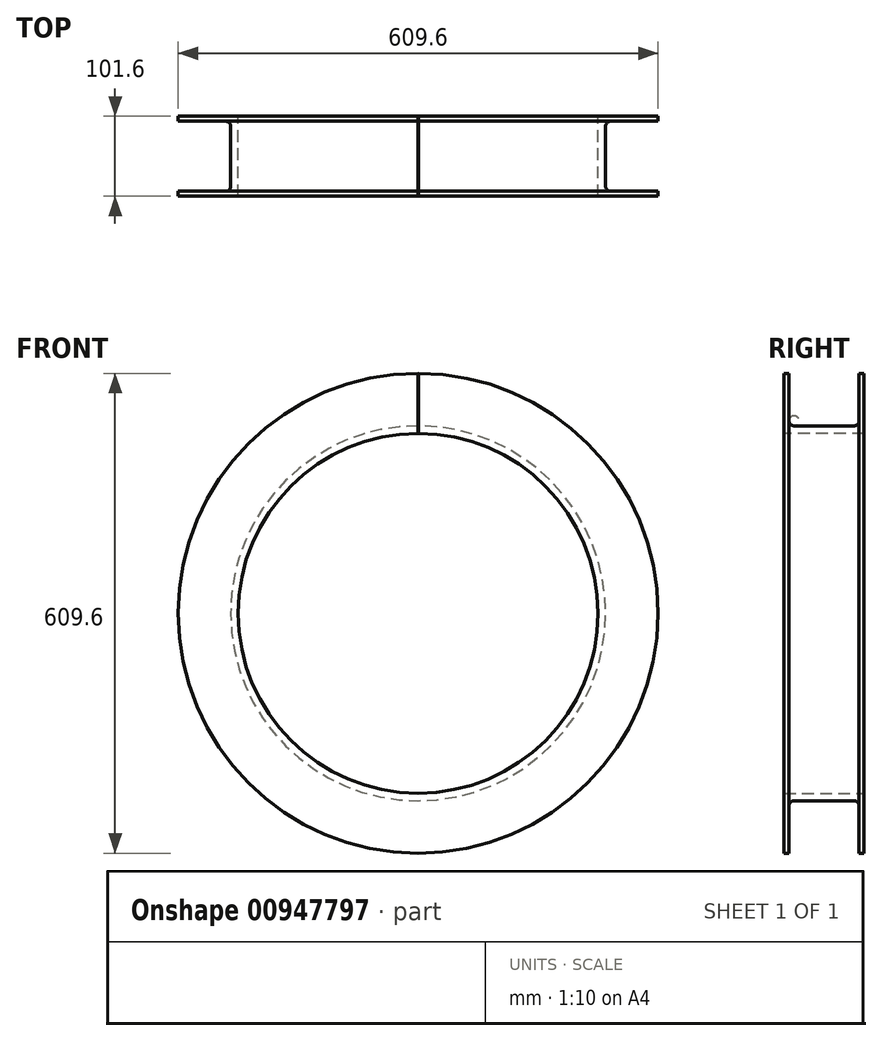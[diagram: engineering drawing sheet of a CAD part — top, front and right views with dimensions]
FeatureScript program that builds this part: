
annotation { "Feature Type Name" : "Feature", "Feature Type Description" : "" }
export const myFeature = defineFeature(function(context is Context, id is Id, definition is map)
    precondition{}
    {
        {
            var Q0;
            Q0=qCreatedBy(makeId("Right.planeOp"),FACE);
            var sketch = newSketch(context, id + "F0", { "sketchPlane" : qUnion([Q0])});
            skLineSegment(sketch, "E0", {"start": v(-118.17, 304.8) * mm, "end": v(123.28, 304.8) * mm, "construction": true});
            skLineSegment(sketch, "E1", {"start": v(0, 0) * mm, "end": v(0, 304.8) * mm, "construction": true});
            skLineSegment(sketch, "E2", {"start": v(0, 0) * mm, "end": v(-432.22, 0) * mm, "construction": true});
            skLineSegment(sketch, "E3.bottom", {"start": v(50.8, 228.6) * mm, "end": v(-50.8, 228.6) * mm});
            skLineSegment(sketch, "E3.left", {"start": v(50.8, 228.6) * mm, "end": v(50.8, 304.8) * mm});
            skLineSegment(sketch, "E3.right", {"start": v(-50.8, 228.6) * mm, "end": v(-50.8, 304.8) * mm});
            skPoint(sketch, "E3.middle", {"position": v(0, 304.8) * mm});
            skPoint(sketch, "E3.top.end.orphan", {"position": v(-50.8, 381) * mm});
            skPoint(sketch, "E4.orphan", {"position": v(50.8, 381) * mm});
            skLineSegment(sketch, "E5", {"start": v(44.45, 304.8) * mm, "end": v(44.45, 244.48) * mm});
            skLineSegment(sketch, "E6", {"start": v(38.1, 238.13) * mm, "end": v(-38.1, 238.13) * mm});
            skLineSegment(sketch, "E7", {"start": v(-44.45, 244.48) * mm, "end": v(-44.45, 304.8) * mm});
            skPoint(sketch, "E8.visualSharp", {"position": v(-44.45, 238.13) * mm});
            skArc(sketch, "E8.filletArc", {"start": v(-44.45, 244.48) * mm, "mid": v(-42.6, 239.98) * mm, "end": v(-38.1, 238.13) * mm});
            skPoint(sketch, "E9.visualSharp", {"position": v(44.45, 238.13) * mm});
            skArc(sketch, "E9.filletArc", {"start": v(38.1, 238.13) * mm, "mid": v(42.6, 239.98) * mm, "end": v(44.45, 244.48) * mm});
            skLineSegment(sketch, "E10", {"start": v(-50.8, 304.8) * mm, "end": v(-44.45, 304.8) * mm});
            skLineSegment(sketch, "E11", {"start": v(44.45, 304.8) * mm, "end": v(50.8, 304.8) * mm});
            skSolve(sketch);
        }
        {
            var Q0;
            Q0 = qSketchRegion(id + "F0", true);
            var Q1;
            Q1=sQuery(id+"F0.wireOp",EDGE,"E2");
            revolve(context, id + "F1", {"surfaceOperationType" : NewSurfaceOperationType.NEW, "entities" : qUnion([Q0]), "axis" : qUnion([Q1]), "revolveType" : RevolveType.ONE_DIRECTION, "angle" : 359.9 * degree});
        }
    });
